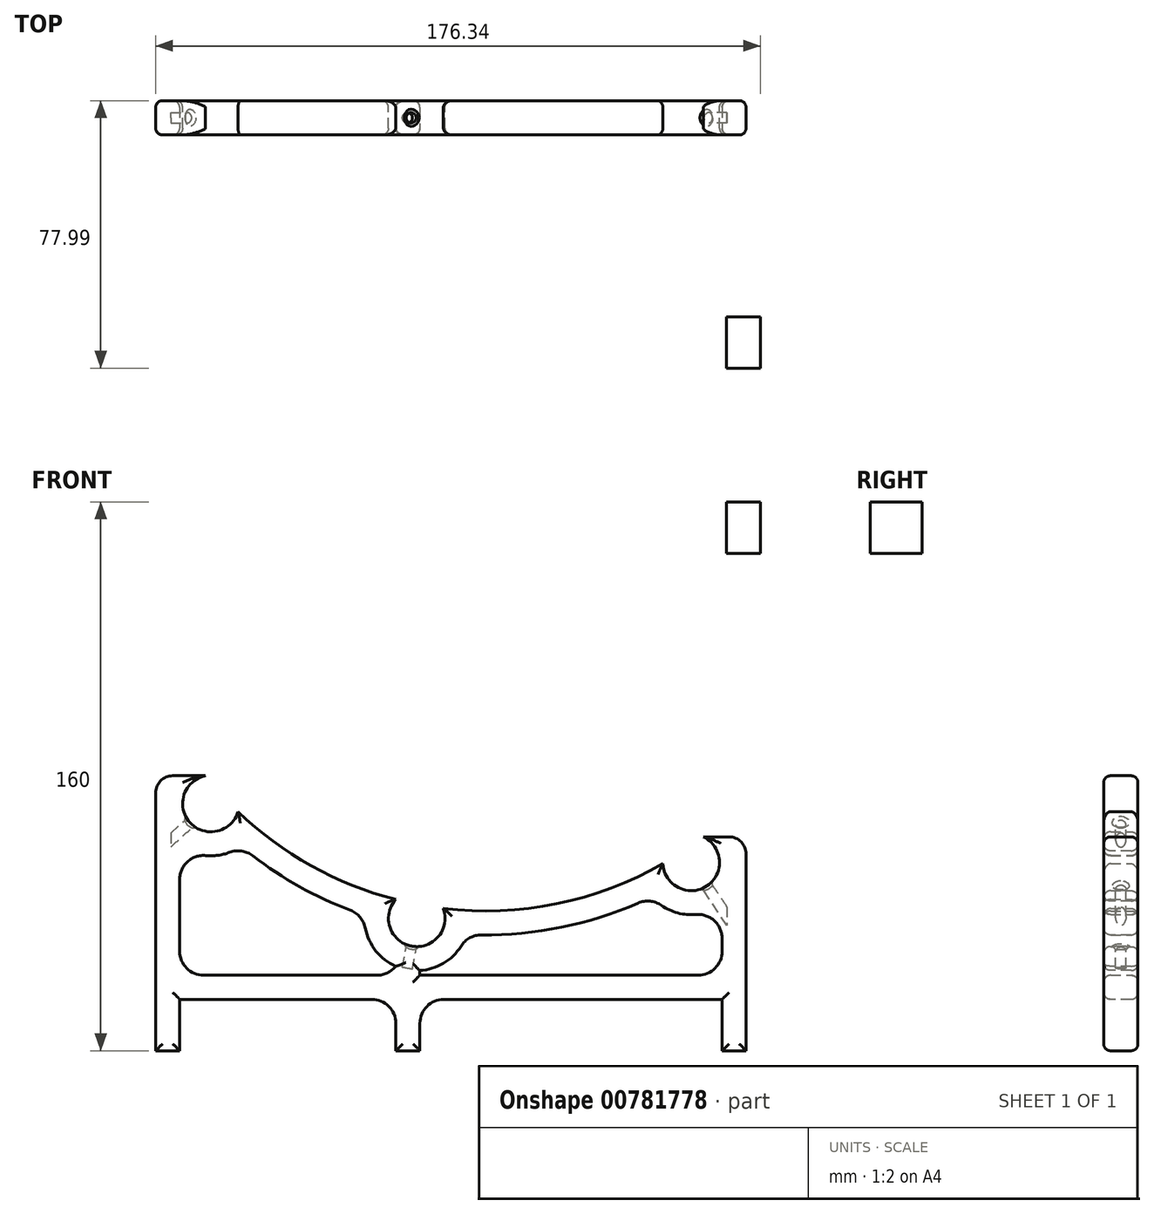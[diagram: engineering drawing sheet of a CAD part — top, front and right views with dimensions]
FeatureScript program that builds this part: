
annotation { "Feature Type Name" : "Feature", "Feature Type Description" : "" }
export const myFeature = defineFeature(function(context is Context, id is Id, definition is map)
    precondition{}
    {
        {
            var Q0;
            Q0=qCreatedBy(makeId("Front.planeOp"),FACE);
            var sketch = newSketch(context, id + "F0", { "sketchPlane" : qUnion([Q0])});
            skCircle(sketch, "E0", {"center": v(0, 0) * mm, "radius": 100 * mm, "construction": true});
            skLineSegment(sketch, "E1", {"start": v(-89.15, -130) * mm, "end": v(130.91, -130) * mm, "construction": true});
            skCircle(sketch, "E2", {"center": v(-80, -72.93) * mm, "radius": 8.25 * mm});
            skCircle(sketch, "E3", {"center": v(-20, -106.39) * mm, "radius": 8.25 * mm});
            skCircle(sketch, "E4", {"center": v(60, -90.1) * mm, "radius": 8.25 * mm});
            skCircle(sketch, "E5", {"center": v(5.53, -27.15) * mm, "radius": 75 * mm, "construction": true});
            skLineSegment(sketch, "E6", {"start": v(-96.11, -69.84) * mm, "end": v(-96.11, -130) * mm});
            skLineSegment(sketch, "E7", {"start": v(-96.11, -130) * mm, "end": v(76, -130) * mm});
            skLineSegment(sketch, "E8", {"start": v(76, -130) * mm, "end": v(76, -87.64) * mm});
            skCircle(sketch, "E9", {"center": v(0, 0) * mm, "radius": 104.24 * mm});
            skLineSegment(sketch, "E10", {"start": v(-91.11, -64.84) * mm, "end": v(-81.62, -64.84) * mm});
            skLineSegment(sketch, "E11", {"start": v(71, -82.64) * mm, "end": v(63.53, -82.64) * mm});
            skLineSegment(sketch, "E12", {"start": v(-81.19, -59.38) * mm, "end": v(-67.22, -74.7) * mm, "construction": true});
            skLineSegment(sketch, "E13", {"start": v(-81.62, -64.84) * mm, "end": v(-72.1, -75.29) * mm, "construction": true});
            skPoint(sketch, "E14.visualSharp", {"position": v(-96.11, -64.84) * mm});
            skArc(sketch, "E14.filletArc", {"start": v(-91.11, -64.84) * mm, "mid": v(-94.65, -66.3) * mm, "end": v(-96.11, -69.84) * mm});
            skPoint(sketch, "E15.visualSharp", {"position": v(76, -82.64) * mm});
            skArc(sketch, "E15.filletArc", {"start": v(76, -87.64) * mm, "mid": v(74.53, -84.1) * mm, "end": v(71, -82.64) * mm});
            skSolve(sketch);
        }
        {
            var Q0;
            Q0=makeQuery(id+"F0.imprint","IMPRINT",FACE,{"disambiguationData":[TD([[makeQuery(id+"F0.imprint","IMPRINT",EDGE,{"derivedFrom":sQuery(id+"F0.wireOp",EDGE,"E6")}),1.0]])]});
            extrude(context, id + "F1", {"entities" : qUnion([Q0]), "depth" : 10 * mm, "offsetDistance" : 25 * mm});
        }
        {
            var Q0;
            Q0=makeQuery(id+"F1.opExtrude","CAP_FACE",FACE,{"disambiguationData":[OSD([sQuery(id+"F0.wireOp",EDGE,"E2"),sQuery(id+"F0.wireOp",EDGE,"E3"),sQuery(id+"F0.wireOp",EDGE,"E4"),sQuery(id+"F0.wireOp",EDGE,"E6"),sQuery(id+"F0.wireOp",EDGE,"E7"),sQuery(id+"F0.wireOp",EDGE,"E8"),sQuery(id+"F0.wireOp",EDGE,"E9"),sQuery(id+"F0.wireOp",EDGE,"E10"),sQuery(id+"F0.wireOp",EDGE,"E11")])],"isStart":false});
            shell(context, id + "F2", {"entities" : qUnion([Q0]), "thickness" : 7 * mm});
        }
        {
            var Q0;
            Q0=makeQuery(id+"F2.opShell","OFFSET_FACE",FACE,{"disambiguationData":[OSD([sQuery(id+"F0.wireOp",EDGE,"E2"),sQuery(id+"F0.wireOp",EDGE,"E3"),sQuery(id+"F0.wireOp",EDGE,"E4"),sQuery(id+"F0.wireOp",EDGE,"E6"),sQuery(id+"F0.wireOp",EDGE,"E7"),sQuery(id+"F0.wireOp",EDGE,"E8"),sQuery(id+"F0.wireOp",EDGE,"E9"),sQuery(id+"F0.wireOp",EDGE,"E10"),sQuery(id+"F0.wireOp",EDGE,"E11")]),OD(0.0)]});
            extrude(context, id + "F3", {"entities" : qUnion([Q0]), "operationType" : NewBodyOperationType.REMOVE, "oppositeDirection" : true, "depth" : 25 * mm, "offsetDistance" : 25 * mm, "symmetric" : true});
        }
        {
            var Q0;
            Q0=makeQuery(id+"F1.opExtrude","CAP_FACE",FACE,{"disambiguationData":[OSD([sQuery(id+"F0.wireOp",EDGE,"E2"),sQuery(id+"F0.wireOp",EDGE,"E3"),sQuery(id+"F0.wireOp",EDGE,"E4"),sQuery(id+"F0.wireOp",EDGE,"E6"),sQuery(id+"F0.wireOp",EDGE,"E7"),sQuery(id+"F0.wireOp",EDGE,"E8"),sQuery(id+"F0.wireOp",EDGE,"E9"),sQuery(id+"F0.wireOp",EDGE,"E10"),sQuery(id+"F0.wireOp",EDGE,"E11"),sQuery(id+"F0.wireOp",EDGE,"E14.filletArc"),sQuery(id+"F0.wireOp",EDGE,"E15.filletArc")])],"isStart":false});
            var sketch = newSketch(context, id + "F4", { "sketchPlane" : qUnion([Q0])});
            skLineSegment(sketch, "E16", {"start": v(-26.11, -123) * mm, "end": v(-26.11, -120.36) * mm});
            skLineSegment(sketch, "E17", {"start": v(-19.11, -121.61) * mm, "end": v(-19.11, -123) * mm});
            skLineSegment(sketch, "E18.bottom", {"start": v(-96.11, -130) * mm, "end": v(-89.11, -130) * mm});
            skLineSegment(sketch, "E18.top", {"start": v(-96.11, -145) * mm, "end": v(-89.11, -145) * mm});
            skLineSegment(sketch, "E18.left", {"start": v(-96.11, -130) * mm, "end": v(-96.11, -145) * mm});
            skLineSegment(sketch, "E18.right", {"start": v(-89.11, -130) * mm, "end": v(-89.11, -145) * mm});
            skLineSegment(sketch, "E19.bottom", {"start": v(-26.11, -123) * mm, "end": v(-19.08, -123) * mm});
            skLineSegment(sketch, "E19.top", {"start": v(-26.11, -145) * mm, "end": v(-19.08, -145) * mm});
            skLineSegment(sketch, "E19.left", {"start": v(-26.11, -123) * mm, "end": v(-26.11, -145) * mm});
            skLineSegment(sketch, "E19.right", {"start": v(-19.08, -123) * mm, "end": v(-19.08, -145) * mm});
            skLineSegment(sketch, "E20.bottom", {"start": v(76, -130) * mm, "end": v(69, -130) * mm});
            skLineSegment(sketch, "E20.top", {"start": v(76, -145) * mm, "end": v(69, -145) * mm});
            skLineSegment(sketch, "E20.left", {"start": v(76, -130) * mm, "end": v(76, -145) * mm});
            skLineSegment(sketch, "E20.right", {"start": v(69, -130) * mm, "end": v(69, -145) * mm});
            skSolve(sketch);
        }
        {
            var Q0;
            Q0 = qSketchRegion(id + "F4", true);
            var Q1;
            {var subQ0=sQuery(id+"F4.wireOp",EDGE,"E16");Q1=makeQuery(id+"F4.imprint","IMPRINT",FACE,{"disambiguationData":[TD([[makeQuery(id+"F4.imprint","IMPRINT",EDGE,{"derivedFrom":subQ0}),-1.0]])]});}
            var Q2;
            Q2=makeQuery(id+"F1.opExtrude","CAP_FACE",FACE,{"disambiguationData":[OSD([sQuery(id+"F0.wireOp",EDGE,"E2"),sQuery(id+"F0.wireOp",EDGE,"E3"),sQuery(id+"F0.wireOp",EDGE,"E4"),sQuery(id+"F0.wireOp",EDGE,"E6"),sQuery(id+"F0.wireOp",EDGE,"E7"),sQuery(id+"F0.wireOp",EDGE,"E8"),sQuery(id+"F0.wireOp",EDGE,"E9"),sQuery(id+"F0.wireOp",EDGE,"E10"),sQuery(id+"F0.wireOp",EDGE,"E11"),sQuery(id+"F0.wireOp",EDGE,"E14.filletArc"),sQuery(id+"F0.wireOp",EDGE,"E15.filletArc")])],"isStart":true});
            extrude(context, id + "F5", {"entities" : qUnion([Q0, Q1]), "operationType" : NewBodyOperationType.ADD, "endBound" : BoundingType.UP_TO_SURFACE, "oppositeDirection" : true, "depth" : 25 * mm, "endBoundEntityFace" : qUnion([Q2]), "offsetDistance" : 25 * mm});
        }
        {
            var Q0;
            {var subQ0=sQuery(id+"F0.wireOp",EDGE,"E7");Q0=makeQuery(id+"F5.boolean.opBoolean","INTERSECT",EDGE,{"derivedFrom":[makeQuery(id+"F3.boolean.opBoolean","MERGE",FACE,{"derivedFrom":[makeQuery(id+"F2.opShell","OFFSET_FACE",FACE,{"disambiguationData":[OSD([subQ0])]})],"fromTools":[makeQuery(id+"F3.opExtrude","SWEPT_FACE",FACE,{"disambiguationData":[OSD([subQ0])]})]}),makeQuery(id+"F5.opExtrude","SWEPT_FACE",FACE,{"disambiguationData":[OSD([sQuery(id+"F4.wireOp",EDGE,"E16"),sQuery(id+"F4.wireOp",EDGE,"E19.left")])]})]});}
            var Q1;
            Q1=makeQuery(id+"F5.opExtrude","SWEPT_EDGE",EDGE,{"disambiguationData":[OSD([sQuery(id+"F0.wireOp",EDGE,"E3"),sQuery(id+"F4.wireOp",EDGE,"E16")])]});
            var Q2;
            Q2=makeQuery(id+"F5.opExtrude","SWEPT_EDGE",EDGE,{"disambiguationData":[OSD([sQuery(id+"F0.wireOp",EDGE,"E3"),sQuery(id+"F4.wireOp",EDGE,"E17")])]});
            var Q3;
            Q3=makeQuery(id+"F5.opExtrude","SWEPT_EDGE",EDGE,{"disambiguationData":[OSD([sQuery(id+"F4.wireOp",EDGE,"E17"),sQuery(id+"F4.wireOp",EDGE,"E19.bottom")])]});
            var Q4;
            {var subQ0=sQuery(id+"F0.wireOp",EDGE,"E9");var subQ1=sQuery(id+"F0.wireOp",EDGE,"E3");var subQ2=makeQuery(id+"F0.imprint","INTERSECT",VERTEX,{"disambiguationData":[OD(0.0)],"derivedFrom":[subQ1,subQ0]});Q4=makeQuery(id+"F3.boolean.opBoolean","MERGE",EDGE,{"derivedFrom":[makeQuery(id+"F2.opShell","OFFSET_EDGE",EDGE,{"disambiguationData":[OSD([subQ1,subQ0]),TDD([makeQuery(id+"F1.opExtrude","SWEPT_EDGE",EDGE,{"disambiguationData":[OSD([subQ1,subQ0]),TDD([subQ2])]})])]}),makeQuery(id+"F3.opExtrude","SWEPT_EDGE",EDGE,{"disambiguationData":[OSD([subQ1,subQ0]),TDD([makeQuery(id+"F2.opShell","OFFSET_VERTEX",VERTEX,{"disambiguationData":[OSD([subQ1,subQ0]),TDD([makeQuery(id+"F1.opExtrude","CAP_VERTEX",VERTEX,{"disambiguationData":[OSD([subQ1,subQ0]),TDD([subQ2])],"isStart":true})])]})])]})]});}
            var Q5;
            {var subQ0=sQuery(id+"F0.wireOp",EDGE,"E9");var subQ1=sQuery(id+"F0.wireOp",EDGE,"E2");Q5=makeQuery(id+"F3.boolean.opBoolean","MERGE",EDGE,{"derivedFrom":[makeQuery(id+"F2.opShell","OFFSET_EDGE",EDGE,{"disambiguationData":[OSD([subQ1,subQ0])]}),makeQuery(id+"F3.opExtrude","SWEPT_EDGE",EDGE,{"disambiguationData":[OSD([subQ1,subQ0])]})]});}
            var Q6;
            {var subQ0=sQuery(id+"F0.wireOp",EDGE,"E6");var subQ1=makeQuery(id+"F1.opExtrude","SWEPT_FACE",FACE,{"disambiguationData":[OSD([subQ0])]});var subQ2=sQuery(id+"F0.wireOp",EDGE,"E15.filletArc");var subQ3=sQuery(id+"F0.wireOp",EDGE,"E14.filletArc");var subQ4=sQuery(id+"F0.wireOp",EDGE,"E11");var subQ5=sQuery(id+"F0.wireOp",EDGE,"E10");var subQ6=sQuery(id+"F0.wireOp",EDGE,"E9");var subQ7=sQuery(id+"F0.wireOp",EDGE,"E8");var subQ8=sQuery(id+"F0.wireOp",EDGE,"E7");var subQ9=sQuery(id+"F0.wireOp",EDGE,"E4");var subQ10=sQuery(id+"F0.wireOp",EDGE,"E3");var subQ11=sQuery(id+"F0.wireOp",EDGE,"E2");var subQ12=makeQuery(id+"F1.opExtrude","SWEPT_FACE",FACE,{"disambiguationData":[OSD([subQ11])]});Q6=makeQuery(id+"F3.boolean.opBoolean","MERGE",EDGE,{"derivedFrom":[makeQuery(id+"F2.opShell","TWEAK_EDGE",EDGE,{"derivedFrom":[subQ12,subQ1]}),makeQuery(id+"F3.opExtrude","SWEPT_EDGE",EDGE,{"disambiguationData":[OSD([subQ11,subQ10,subQ9,subQ0,subQ8,subQ7,subQ6,subQ5,subQ4,subQ3,subQ2]),TDD([makeQuery(id+"F2.opShell","TWEAK_VERTEX",VERTEX,{"derivedFrom":[subQ12,makeQuery(id+"F1.opExtrude","CAP_FACE",FACE,{"disambiguationData":[OSD([subQ11,subQ10,subQ9,subQ0,subQ8,subQ7,subQ6,subQ5,subQ4,subQ3,subQ2])],"isStart":true}),subQ1]})])]})]});}
            var Q7;
            {var subQ0=sQuery(id+"F0.wireOp",EDGE,"E9");var subQ1=sQuery(id+"F0.wireOp",EDGE,"E3");var subQ2=makeQuery(id+"F0.imprint","INTERSECT",VERTEX,{"disambiguationData":[OD(1.0)],"derivedFrom":[subQ1,subQ0]});Q7=makeQuery(id+"F3.boolean.opBoolean","MERGE",EDGE,{"derivedFrom":[makeQuery(id+"F2.opShell","OFFSET_EDGE",EDGE,{"disambiguationData":[OSD([subQ1,subQ0]),TDD([makeQuery(id+"F1.opExtrude","SWEPT_EDGE",EDGE,{"disambiguationData":[OSD([subQ1,subQ0]),TDD([subQ2])]})])]}),makeQuery(id+"F3.opExtrude","SWEPT_EDGE",EDGE,{"disambiguationData":[OSD([subQ1,subQ0]),TDD([makeQuery(id+"F2.opShell","OFFSET_VERTEX",VERTEX,{"disambiguationData":[OSD([subQ1,subQ0]),TDD([makeQuery(id+"F1.opExtrude","CAP_VERTEX",VERTEX,{"disambiguationData":[OSD([subQ1,subQ0]),TDD([subQ2])],"isStart":true})])]})])]})]});}
            var Q8;
            {var subQ0=sQuery(id+"F0.wireOp",EDGE,"E9");var subQ1=sQuery(id+"F0.wireOp",EDGE,"E4");Q8=makeQuery(id+"F3.boolean.opBoolean","MERGE",EDGE,{"derivedFrom":[makeQuery(id+"F2.opShell","OFFSET_EDGE",EDGE,{"disambiguationData":[OSD([subQ1,subQ0])]}),makeQuery(id+"F3.opExtrude","SWEPT_EDGE",EDGE,{"disambiguationData":[OSD([subQ1,subQ0])]})]});}
            var Q9;
            {var subQ0=sQuery(id+"F0.wireOp",EDGE,"E8");var subQ1=makeQuery(id+"F1.opExtrude","SWEPT_FACE",FACE,{"disambiguationData":[OSD([subQ0])]});var subQ2=sQuery(id+"F0.wireOp",EDGE,"E4");var subQ3=makeQuery(id+"F1.opExtrude","SWEPT_FACE",FACE,{"disambiguationData":[OSD([subQ2])]});var subQ4=sQuery(id+"F0.wireOp",EDGE,"E15.filletArc");var subQ5=sQuery(id+"F0.wireOp",EDGE,"E14.filletArc");var subQ6=sQuery(id+"F0.wireOp",EDGE,"E11");var subQ7=sQuery(id+"F0.wireOp",EDGE,"E10");var subQ8=sQuery(id+"F0.wireOp",EDGE,"E9");var subQ9=sQuery(id+"F0.wireOp",EDGE,"E7");var subQ10=sQuery(id+"F0.wireOp",EDGE,"E6");var subQ11=sQuery(id+"F0.wireOp",EDGE,"E3");var subQ12=sQuery(id+"F0.wireOp",EDGE,"E2");Q9=makeQuery(id+"F3.boolean.opBoolean","MERGE",EDGE,{"derivedFrom":[makeQuery(id+"F2.opShell","TWEAK_EDGE",EDGE,{"derivedFrom":[subQ3,subQ1]}),makeQuery(id+"F3.opExtrude","SWEPT_EDGE",EDGE,{"disambiguationData":[OSD([subQ12,subQ11,subQ2,subQ10,subQ9,subQ0,subQ8,subQ7,subQ6,subQ5,subQ4]),TDD([makeQuery(id+"F2.opShell","TWEAK_VERTEX",VERTEX,{"derivedFrom":[makeQuery(id+"F1.opExtrude","CAP_FACE",FACE,{"disambiguationData":[OSD([subQ12,subQ11,subQ2,subQ10,subQ9,subQ0,subQ8,subQ7,subQ6,subQ5,subQ4])],"isStart":true}),subQ3,subQ1]})])]})]});}
            var Q10;
            {var subQ0=sQuery(id+"F0.wireOp",EDGE,"E7");var subQ1=sQuery(id+"F0.wireOp",EDGE,"E6");Q10=makeQuery(id+"F3.boolean.opBoolean","MERGE",EDGE,{"derivedFrom":[makeQuery(id+"F2.opShell","OFFSET_EDGE",EDGE,{"disambiguationData":[OSD([subQ1,subQ0])]}),makeQuery(id+"F3.opExtrude","SWEPT_EDGE",EDGE,{"disambiguationData":[OSD([subQ1,subQ0])]})]});}
            var Q11;
            {var subQ0=sQuery(id+"F0.wireOp",EDGE,"E8");var subQ1=sQuery(id+"F0.wireOp",EDGE,"E7");Q11=makeQuery(id+"F3.boolean.opBoolean","MERGE",EDGE,{"derivedFrom":[makeQuery(id+"F2.opShell","OFFSET_EDGE",EDGE,{"disambiguationData":[OSD([subQ1,subQ0])]}),makeQuery(id+"F3.opExtrude","SWEPT_EDGE",EDGE,{"disambiguationData":[OSD([subQ1,subQ0])]})]});}
            var Q12;
            Q12=makeQuery(id+"F5.opExtrude","SWEPT_EDGE",EDGE,{"disambiguationData":[OSD([sQuery(id+"F0.wireOp",EDGE,"E7"),sQuery(id+"F4.wireOp",EDGE,"E20.bottom"),sQuery(id+"F4.wireOp",EDGE,"E20.right")])]});
            var Q13;
            Q13=makeQuery(id+"F5.boolean.opBoolean","INTERSECT",EDGE,{"derivedFrom":[makeQuery(id+"F1.opExtrude","SWEPT_FACE",FACE,{"disambiguationData":[OSD([sQuery(id+"F0.wireOp",EDGE,"E7")])]}),makeQuery(id+"F5.opExtrude","SWEPT_FACE",FACE,{"disambiguationData":[OSD([sQuery(id+"F4.wireOp",EDGE,"E16"),sQuery(id+"F4.wireOp",EDGE,"E19.left")])]})]});
            var Q14;
            Q14=makeQuery(id+"F5.opExtrude","SWEPT_EDGE",EDGE,{"disambiguationData":[OSD([sQuery(id+"F0.wireOp",EDGE,"E7"),sQuery(id+"F4.wireOp",EDGE,"E18.bottom"),sQuery(id+"F4.wireOp",EDGE,"E18.right")])]});
            var Q15;
            Q15=makeQuery(id+"F5.boolean.opBoolean","INTERSECT",EDGE,{"derivedFrom":[makeQuery(id+"F1.opExtrude","SWEPT_FACE",FACE,{"disambiguationData":[OSD([sQuery(id+"F0.wireOp",EDGE,"E7")])]}),makeQuery(id+"F5.opExtrude","SWEPT_FACE",FACE,{"disambiguationData":[OSD([sQuery(id+"F4.wireOp",EDGE,"E19.right")])]})]});
            fillet(context, id + "F6", {"entities" : qUnion([Q0, Q1, Q2, Q3, Q4, Q5, Q6, Q7, Q8, Q9, Q10, Q11, Q12, Q13, Q14, Q15]), "radius" : 7 * mm, "tangentPropagation" : true, "allowEdgeOverflow" : false});
        }
        {
            var Q0;
            Q0=makeQuery(id+"F1.opExtrude","SWEPT_EDGE",EDGE,{"disambiguationData":[OSD([sQuery(id+"F0.wireOp",EDGE,"E2"),sQuery(id+"F0.wireOp",EDGE,"E9"),sQuery(id+"F0.wireOp",EDGE,"E10")])]});
            var Q1;
            Q1=makeQuery(id+"F1.opExtrude","SWEPT_EDGE",EDGE,{"disambiguationData":[OSD([sQuery(id+"F0.wireOp",EDGE,"E2"),sQuery(id+"F0.wireOp",EDGE,"E9")])]});
            cPlane(context, id + "F7", {"entities" : qUnion([Q0, Q1]), "cplaneType" : CPlaneType.LINE_ANGLE, "offset" : 25 * mm, "angle" : 0 * degree, "oppositeDirection" : true, "width" : 150 * mm, "height" : 150 * mm});
        }
        {
            var Q0;
            Q0=qCreatedBy(id+"F7.planeOp",FACE);
            var sketch = newSketch(context, id + "F8", { "sketchPlane" : qUnion([Q0])});
            skLineSegment(sketch, "E21.0", {"start": v(10, 7.07) * mm, "end": v(0, 7.07) * mm, "construction": true});
            skLineSegment(sketch, "E22.0", {"start": v(10, -7.07) * mm, "end": v(0, -7.07) * mm, "construction": true});
            skLineSegment(sketch, "E23", {"start": v(10, 7.07) * mm, "end": v(0, -7.07) * mm, "construction": true});
            skLineSegment(sketch, "E24", {"start": v(0, 7.07) * mm, "end": v(10, -7.07) * mm, "construction": true});
            skCircle(sketch, "E25", {"center": v(5, 0) * mm, "radius": 1.5 * mm});
            skSolve(sketch);
        }
        {
            var Q0;
            Q0=makeQuery(id+"F8.imprint","IMPRINT",FACE,{"disambiguationData":[TD([[makeQuery(id+"F8.imprint","IMPRINT",EDGE,{"derivedFrom":sQuery(id+"F8.wireOp",EDGE,"E25")}),1.0]])]});
            var Q1;
            Q1=makeQuery(id+"F1.opExtrude","SWEPT_FACE",FACE,{"disambiguationData":[OSD([sQuery(id+"F0.wireOp",EDGE,"E6")])]});
            extrude(context, id + "F9", {"entities" : qUnion([Q0]), "operationType" : NewBodyOperationType.REMOVE, "endBound" : BoundingType.UP_TO_SURFACE, "depth" : 25 * mm, "endBoundEntityFace" : qUnion([Q1]), "hasOffset" : true, "offsetDistance" : 6 * mm});
        }
        {
            var Q0;
            {var subQ0=sQuery(id+"F0.wireOp",EDGE,"E9");var subQ1=sQuery(id+"F0.wireOp",EDGE,"E3");Q0=makeQuery(id+"F1.opExtrude","SWEPT_EDGE",EDGE,{"disambiguationData":[OSD([subQ1,subQ0]),TDD([makeQuery(id+"F0.imprint","INTERSECT",VERTEX,{"disambiguationData":[OD(0.0)],"derivedFrom":[subQ1,subQ0]})])]});}
            var Q1;
            {var subQ0=sQuery(id+"F0.wireOp",EDGE,"E9");var subQ1=sQuery(id+"F0.wireOp",EDGE,"E3");Q1=makeQuery(id+"F1.opExtrude","SWEPT_EDGE",EDGE,{"disambiguationData":[OSD([subQ1,subQ0]),TDD([makeQuery(id+"F0.imprint","INTERSECT",VERTEX,{"disambiguationData":[OD(1.0)],"derivedFrom":[subQ1,subQ0]})])]});}
            cPlane(context, id + "F10", {"entities" : qUnion([Q0, Q1]), "cplaneType" : CPlaneType.LINE_ANGLE, "offset" : 25 * mm, "angle" : 0 * degree, "width" : 150 * mm, "height" : 150 * mm});
        }
        {
            var Q0;
            Q0=qCreatedBy(id+"F10.planeOp",FACE);
            var sketch = newSketch(context, id + "F11", { "sketchPlane" : qUnion([Q0])});
            skLineSegment(sketch, "E26.0", {"start": v(-7.07, 10) * mm, "end": v(-7.07, 0) * mm, "construction": true});
            skLineSegment(sketch, "E27.0", {"start": v(7.07, 10) * mm, "end": v(7.07, 0) * mm, "construction": true});
            skLineSegment(sketch, "E28", {"start": v(-7.07, 0) * mm, "end": v(7.07, 10) * mm, "construction": true});
            skLineSegment(sketch, "E29", {"start": v(7.07, 0) * mm, "end": v(-7.07, 10) * mm, "construction": true});
            skCircle(sketch, "E30", {"center": v(0, 5) * mm, "radius": 1.5 * mm});
            skSolve(sketch);
        }
        {
            var Q0;
            Q0=makeQuery(id+"F11.imprint","IMPRINT",FACE,{"disambiguationData":[TD([[makeQuery(id+"F11.imprint","IMPRINT",EDGE,{"derivedFrom":sQuery(id+"F11.wireOp",EDGE,"E30")}),1.0]])]});
            var Q1;
            Q1=makeQuery(id+"F1.opExtrude","SWEPT_FACE",FACE,{"disambiguationData":[OSD([sQuery(id+"F0.wireOp",EDGE,"E7")])]});
            extrude(context, id + "F12", {"entities" : qUnion([Q0]), "operationType" : NewBodyOperationType.REMOVE, "depth" : 19 * mm, "endBoundEntityFace" : qUnion([Q1]), "hasOffset" : true, "offsetDistance" : 8 * mm});
        }
        {
            var Q0;
            Q0=makeQuery(id+"F1.opExtrude","SWEPT_EDGE",EDGE,{"disambiguationData":[OSD([sQuery(id+"F0.wireOp",EDGE,"E4"),sQuery(id+"F0.wireOp",EDGE,"E9")])]});
            var Q1;
            Q1=makeQuery(id+"F1.opExtrude","SWEPT_EDGE",EDGE,{"disambiguationData":[OSD([sQuery(id+"F0.wireOp",EDGE,"E4"),sQuery(id+"F0.wireOp",EDGE,"E9"),sQuery(id+"F0.wireOp",EDGE,"E11")])]});
            cPlane(context, id + "F13", {"entities" : qUnion([Q0, Q1]), "cplaneType" : CPlaneType.LINE_ANGLE, "offset" : 25 * mm, "angle" : 0 * degree, "width" : 150 * mm, "height" : 150 * mm});
        }
        {
            var Q0;
            Q0=qCreatedBy(id+"F13.planeOp",FACE);
            var sketch = newSketch(context, id + "F14", { "sketchPlane" : qUnion([Q0])});
            skLineSegment(sketch, "E31.0", {"start": v(7.07, 10) * mm, "end": v(7.07, 0) * mm, "construction": true});
            skLineSegment(sketch, "E32.0", {"start": v(-7.07, 10) * mm, "end": v(-7.07, 0) * mm, "construction": true});
            skLineSegment(sketch, "E33", {"start": v(7.07, 0) * mm, "end": v(-7.07, 10) * mm, "construction": true});
            skLineSegment(sketch, "E34", {"start": v(-7.07, 0) * mm, "end": v(7.07, 10) * mm, "construction": true});
            skCircle(sketch, "E35", {"center": v(0, 5) * mm, "radius": 1.5 * mm});
            skSolve(sketch);
        }
        {
            var Q0;
            Q0=makeQuery(id+"F14.imprint","IMPRINT",FACE,{"disambiguationData":[TD([[makeQuery(id+"F14.imprint","IMPRINT",EDGE,{"derivedFrom":sQuery(id+"F14.wireOp",EDGE,"E35")}),1.0]])]});
            var Q1;
            Q1=makeQuery(id+"F1.opExtrude","SWEPT_FACE",FACE,{"disambiguationData":[OSD([sQuery(id+"F0.wireOp",EDGE,"E8")])]});
            extrude(context, id + "F15", {"entities" : qUnion([Q0]), "operationType" : NewBodyOperationType.REMOVE, "endBound" : BoundingType.UP_TO_SURFACE, "depth" : 25 * mm, "endBoundEntityFace" : qUnion([Q1]), "hasOffset" : true, "offsetDistance" : 10 * mm});
        }
        {
            var Q0;
            Q0=makeQuery(id+"F9.boolean.opBoolean","INTERSECT",EDGE,{"derivedFrom":[makeQuery(id+"F1.opExtrude","SWEPT_FACE",FACE,{"disambiguationData":[OSD([sQuery(id+"F0.wireOp",EDGE,"E2")])]}),makeQuery(id+"F9.opExtrude","SWEPT_FACE",FACE,{"disambiguationData":[OSD([sQuery(id+"F8.wireOp",EDGE,"E25")])]})]});
            var Q1;
            Q1=makeQuery(id+"F12.boolean.opBoolean","INTERSECT",EDGE,{"derivedFrom":[makeQuery(id+"F1.opExtrude","SWEPT_FACE",FACE,{"disambiguationData":[OSD([sQuery(id+"F0.wireOp",EDGE,"E3")])]}),makeQuery(id+"F12.opExtrude","SWEPT_FACE",FACE,{"disambiguationData":[OSD([sQuery(id+"F11.wireOp",EDGE,"E30")])]})]});
            var Q2;
            Q2=makeQuery(id+"F15.boolean.opBoolean","INTERSECT",EDGE,{"derivedFrom":[makeQuery(id+"F1.opExtrude","SWEPT_FACE",FACE,{"disambiguationData":[OSD([sQuery(id+"F0.wireOp",EDGE,"E4")])]}),makeQuery(id+"F15.opExtrude","SWEPT_FACE",FACE,{"disambiguationData":[OSD([sQuery(id+"F14.wireOp",EDGE,"E35")])]})]});
            chamfer(context, id + "F16", {"entities" : qUnion([Q0, Q1, Q2]), "width" : 1 * mm, "tangentPropagation" : true});
        }
        {
            var Q0;
            Q0=qCreatedBy(makeId("Top.planeOp"),FACE);
            var sketch = newSketch(context, id + "F17", { "sketchPlane" : qUnion([Q0])});
            skLineSegment(sketch, "E36.bottom", {"start": v(70.23, -63) * mm, "end": v(80.23, -63) * mm});
            skLineSegment(sketch, "E36.top", {"start": v(70.23, -78) * mm, "end": v(80.23, -78) * mm});
            skLineSegment(sketch, "E36.left", {"start": v(70.23, -63) * mm, "end": v(70.23, -78) * mm});
            skLineSegment(sketch, "E36.right", {"start": v(80.23, -63) * mm, "end": v(80.23, -78) * mm});
            skSolve(sketch);
        }
        {
            var Q0;
            Q0 = qSketchRegion(id + "F17", true);
            extrude(context, id + "F18", {"entities" : qUnion([Q0]), "depth" : 15 * mm, "offsetDistance" : 25 * mm});
        }
        {
            var Q0;
            {var subQ0=sQuery(id+"F0.wireOp",EDGE,"E3");Q0=makeQuery(id+"F5.boolean.opBoolean","MERGE",FACE,{"derivedFrom":[makeQuery(id+"F1.opExtrude","CAP_FACE",FACE,{"disambiguationData":[OSD([sQuery(id+"F0.wireOp",EDGE,"E2"),subQ0,sQuery(id+"F0.wireOp",EDGE,"E4"),sQuery(id+"F0.wireOp",EDGE,"E6"),sQuery(id+"F0.wireOp",EDGE,"E7"),sQuery(id+"F0.wireOp",EDGE,"E8"),sQuery(id+"F0.wireOp",EDGE,"E9"),sQuery(id+"F0.wireOp",EDGE,"E10"),sQuery(id+"F0.wireOp",EDGE,"E11"),sQuery(id+"F0.wireOp",EDGE,"E14.filletArc"),sQuery(id+"F0.wireOp",EDGE,"E15.filletArc")])],"isStart":false}),makeQuery(id+"F5.opExtrude","CAP_FACE",FACE,{"disambiguationData":[OSD([subQ0,sQuery(id+"F4.wireOp",EDGE,"E16"),sQuery(id+"F4.wireOp",EDGE,"E17"),sQuery(id+"F4.wireOp",EDGE,"E19.bottom"),sQuery(id+"F4.wireOp",EDGE,"E19.top"),sQuery(id+"F4.wireOp",EDGE,"E19.left"),sQuery(id+"F4.wireOp",EDGE,"E19.right")])],"isStart":true}),makeQuery(id+"F5.opExtrude","CAP_FACE",FACE,{"disambiguationData":[OSD([sQuery(id+"F4.wireOp",EDGE,"E18.bottom"),sQuery(id+"F4.wireOp",EDGE,"E18.top"),sQuery(id+"F4.wireOp",EDGE,"E18.left"),sQuery(id+"F4.wireOp",EDGE,"E18.right")])],"isStart":true}),makeQuery(id+"F5.opExtrude","CAP_FACE",FACE,{"disambiguationData":[OSD([sQuery(id+"F4.wireOp",EDGE,"E20.bottom"),sQuery(id+"F4.wireOp",EDGE,"E20.top"),sQuery(id+"F4.wireOp",EDGE,"E20.left"),sQuery(id+"F4.wireOp",EDGE,"E20.right")])],"isStart":true})]});}
            var Q1;
            {var subQ0=sQuery(id+"F0.wireOp",EDGE,"E3");Q1=makeQuery(id+"F5.boolean.opBoolean","MERGE",FACE,{"derivedFrom":[makeQuery(id+"F1.opExtrude","CAP_FACE",FACE,{"disambiguationData":[OSD([sQuery(id+"F0.wireOp",EDGE,"E2"),subQ0,sQuery(id+"F0.wireOp",EDGE,"E4"),sQuery(id+"F0.wireOp",EDGE,"E6"),sQuery(id+"F0.wireOp",EDGE,"E7"),sQuery(id+"F0.wireOp",EDGE,"E8"),sQuery(id+"F0.wireOp",EDGE,"E9"),sQuery(id+"F0.wireOp",EDGE,"E10"),sQuery(id+"F0.wireOp",EDGE,"E11"),sQuery(id+"F0.wireOp",EDGE,"E14.filletArc"),sQuery(id+"F0.wireOp",EDGE,"E15.filletArc")])],"isStart":true}),makeQuery(id+"F5.opExtrude","CAP_FACE",FACE,{"disambiguationData":[OSD([subQ0,sQuery(id+"F4.wireOp",EDGE,"E16"),sQuery(id+"F4.wireOp",EDGE,"E17"),sQuery(id+"F4.wireOp",EDGE,"E19.bottom"),sQuery(id+"F4.wireOp",EDGE,"E19.top"),sQuery(id+"F4.wireOp",EDGE,"E19.left"),sQuery(id+"F4.wireOp",EDGE,"E19.right")])],"isStart":false}),makeQuery(id+"F5.opExtrude","CAP_FACE",FACE,{"disambiguationData":[OSD([sQuery(id+"F4.wireOp",EDGE,"E18.bottom"),sQuery(id+"F4.wireOp",EDGE,"E18.top"),sQuery(id+"F4.wireOp",EDGE,"E18.left"),sQuery(id+"F4.wireOp",EDGE,"E18.right")])],"isStart":false}),makeQuery(id+"F5.opExtrude","CAP_FACE",FACE,{"disambiguationData":[OSD([sQuery(id+"F4.wireOp",EDGE,"E20.bottom"),sQuery(id+"F4.wireOp",EDGE,"E20.top"),sQuery(id+"F4.wireOp",EDGE,"E20.left"),sQuery(id+"F4.wireOp",EDGE,"E20.right")])],"isStart":false})]});}
            fillet(context, id + "F19", {"entities" : qUnion([Q0, Q1]), "tangentPropagation" : true, "radius" : 2 * mm, "defaultsChanged" : false, "vertexSettings" : [], "allowEdgeOverflow" : false});
        }
    });
